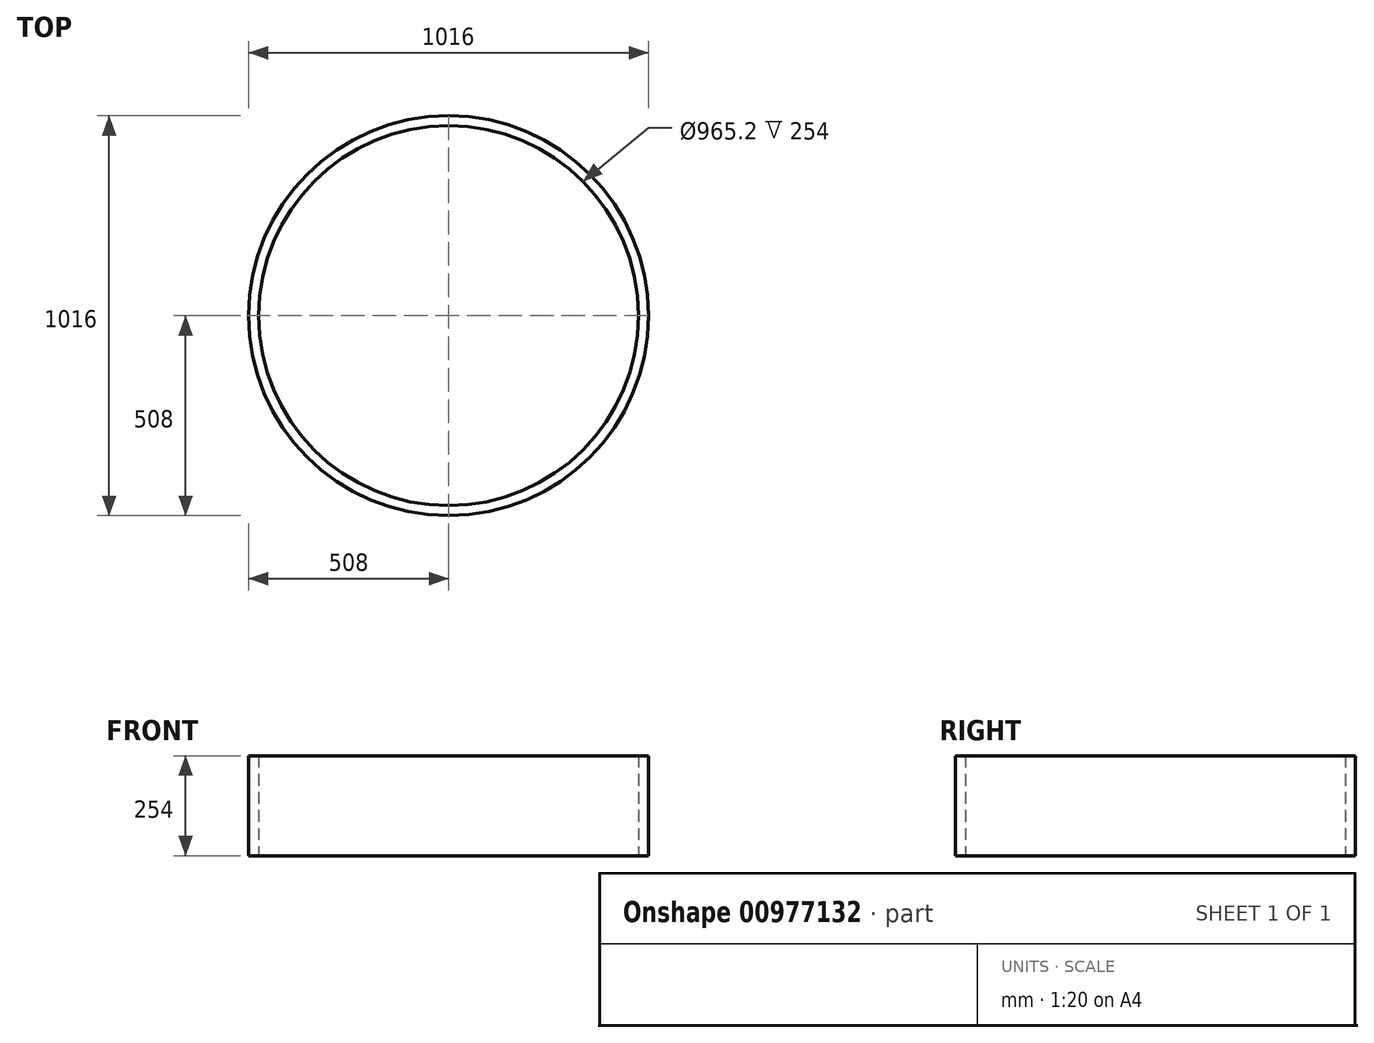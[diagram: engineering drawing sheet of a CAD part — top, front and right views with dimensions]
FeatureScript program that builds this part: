
annotation { "Feature Type Name" : "Feature", "Feature Type Description" : "" }
export const myFeature = defineFeature(function(context is Context, id is Id, definition is map)
    precondition{}
    {
        {
            var Q0;
            Q0=qCreatedBy(makeId("Top.planeOp"),FACE);
            var sketch = newSketch(context, id + "F0", { "sketchPlane" : qUnion([Q0])});
            skCircle(sketch, "E0", {"center": v(0, 0) * mm, "radius": 508 * mm});
            skCircle(sketch, "E1", {"center": v(0, 0) * mm, "radius": 482.6 * mm});
            skSolve(sketch);
        }
        {
            var Q0;
            Q0=makeQuery(id+"F0.imprint","IMPRINT",FACE,{"disambiguationData":[TD([[makeQuery(id+"F0.imprint","IMPRINT",EDGE,{"derivedFrom":sQuery(id+"F0.wireOp",EDGE,"E0")}),1.0]])]});
            extrude(context, id + "F1", {"entities" : qUnion([Q0]), "depth" : 254 * mm, "offsetDistance" : 25.4 * mm});
        }
    });
